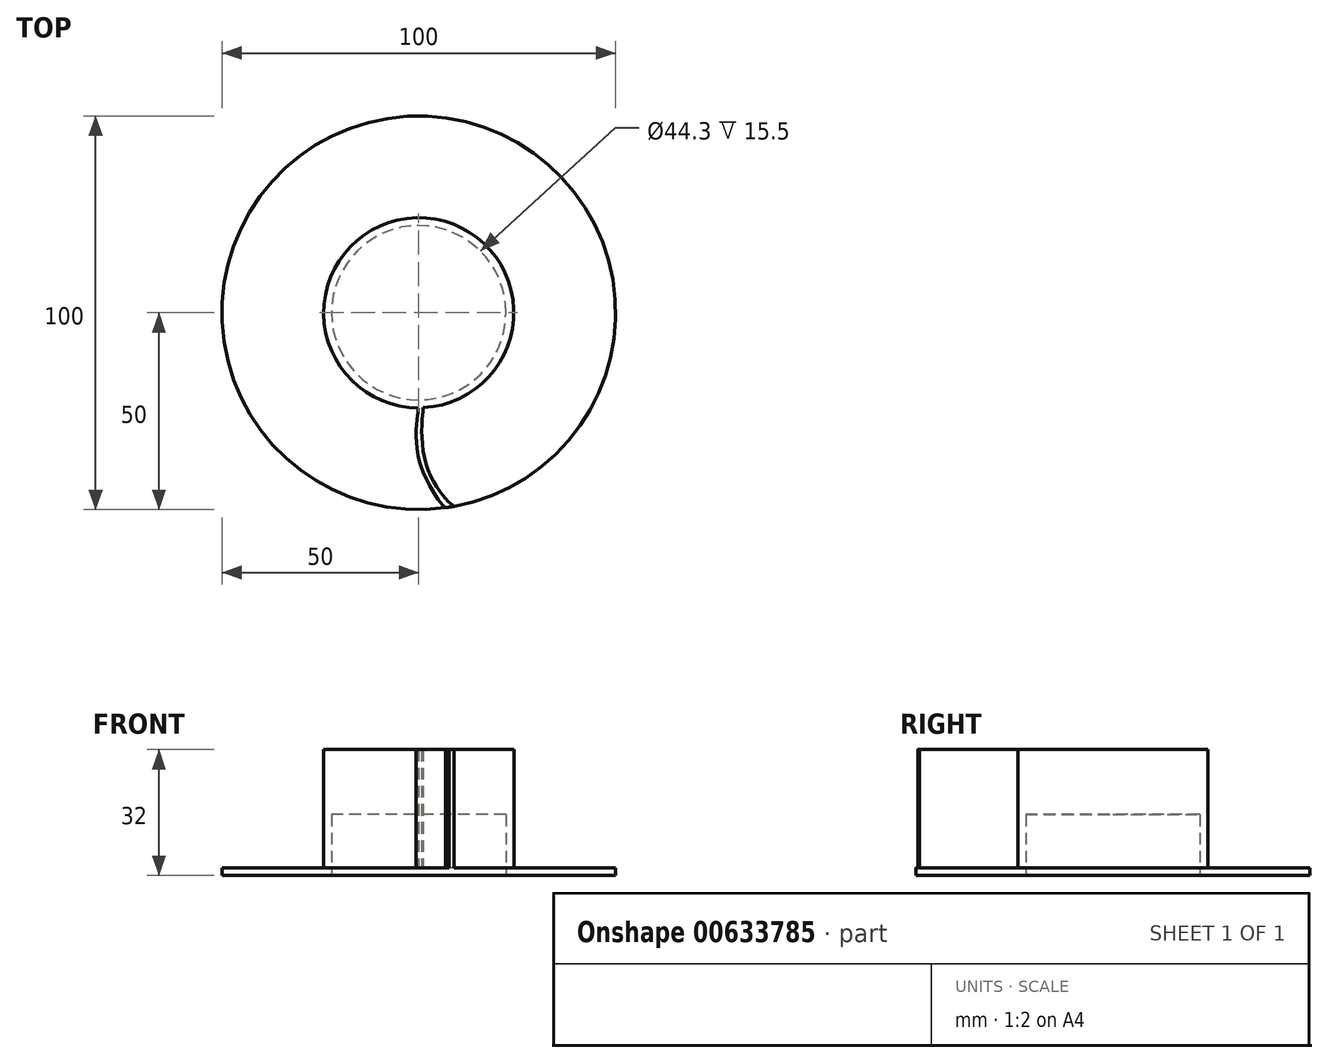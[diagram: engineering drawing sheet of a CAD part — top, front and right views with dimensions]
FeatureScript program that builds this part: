
annotation { "Feature Type Name" : "Feature", "Feature Type Description" : "" }
export const myFeature = defineFeature(function(context is Context, id is Id, definition is map)
    precondition{}
    {
        {
            var Q0;
            Q0=qCreatedBy(makeId("Top.planeOp"),FACE);
            var sketch = newSketch(context, id + "F0", { "sketchPlane" : qUnion([Q0])});
            skCircle(sketch, "E0", {"center": v(0, 0) * mm, "radius": 22.15 * mm});
            skCircle(sketch, "E1.0", {"center": v(0, 0) * mm, "radius": 24.15 * mm});
            skCircle(sketch, "E2", {"center": v(0, 0) * mm, "radius": 50 * mm});
            skSolve(sketch);
        }
        {
            var Q0;
            Q0=makeQuery(id+"F0.imprint","IMPRINT",FACE,{"disambiguationData":[TD([[makeQuery(id+"F0.imprint","IMPRINT",EDGE,{"derivedFrom":sQuery(id+"F0.wireOp",EDGE,"E0")}),-1.0]])]});
            var Q1;
            Q1=makeQuery(id+"F0.imprint","IMPRINT",FACE,{"disambiguationData":[TD([[makeQuery(id+"F0.imprint","IMPRINT",EDGE,{"derivedFrom":sQuery(id+"F0.wireOp",EDGE,"E0")}),1.0]])]});
            extrude(context, id + "F1", {"entities" : qUnion([Q0, Q1]), "depth" : 17 * mm, "offsetDistance" : 25 * mm});
        }
        {
            var Q0;
            Q0=makeQuery(id+"F0.imprint","IMPRINT",FACE,{"disambiguationData":[TD([[makeQuery(id+"F0.imprint","IMPRINT",EDGE,{"derivedFrom":sQuery(id+"F0.wireOp",EDGE,"E0")}),1.0]])]});
            extrude(context, id + "F2", {"entities" : qUnion([Q0]), "operationType" : NewBodyOperationType.REMOVE, "depth" : 15.5 * mm, "offsetDistance" : 25 * mm});
        }
        {
            var Q0;
            Q0=makeQuery(id+"F0.imprint","IMPRINT",FACE,{"disambiguationData":[TD([[makeQuery(id+"F0.imprint","IMPRINT",EDGE,{"derivedFrom":sQuery(id+"F0.wireOp",EDGE,"E1.0")}),-1.0]])]});
            extrude(context, id + "F3", {"entities" : qUnion([Q0]), "operationType" : NewBodyOperationType.ADD, "depth" : 2 * mm, "offsetDistance" : 25 * mm});
        }
        {
            var Q0;
            Q0=makeQuery(id+"F3.opExtrude","CAP_FACE",FACE,{"disambiguationData":[OSD([sQuery(id+"F0.wireOp",EDGE,"E1.0"),sQuery(id+"F0.wireOp",EDGE,"E2")])],"isStart":false});
            var sketch = newSketch(context, id + "F4", { "sketchPlane" : qUnion([Q0])});
            skFitSpline(sketch, "E3", {"points": [v(0, -24.15) * mm, v(-0.02, -24.17) * mm, v(0, -36.96) * mm, v(6.75, -49.54) * mm, v(6.98, -49.51) * mm, v(8.9, -49.2) * mm, v(8.36, -48.7) * mm, v(1.49, -37.1) * mm, v(1.14, -24.12) * mm, v(1.11, -24.08) * mm, v(0, -24.15) * mm]});
            skSolve(sketch);
        }
        {
            var Q0;
            {var subQ0=sQuery(id+"F4.wireOp",EDGE,"E3");var subQ1=makeQuery(id+"F3.opExtrude","CAP_EDGE",EDGE,{"disambiguationData":[OSD([sQuery(id+"F0.wireOp",EDGE,"E2")])],"isStart":false});var subQ2=makeQuery(id+"F4.imprint","INTERSECT",VERTEX,{"disambiguationData":[OD(0.0)],"derivedFrom":[subQ1,subQ0]});Q0=makeQuery(id+"F4.imprint","IMPRINT",FACE,{"disambiguationData":[TD([[makeQuery(id+"F4.imprint","IMPRINT",EDGE,{"disambiguationData":[TD([[subQ2,1.0]])],"derivedFrom":subQ0}),1.0]])]});}
            var Q1;
            Q1=makeQuery(id+"FbTs9hMTHk68URn_1.1.F4.imprint","IMPRINT",FACE,{"disambiguationData":[TD([[makeQuery(id+"FbTs9hMTHk68URn_1.1.F4.imprint","IMPRINT",EDGE,{"derivedFrom":sQuery(id+"FbTs9hMTHk68URn_1.1.F4.wireOp",EDGE,"E3")}),1.0]])]});
            var Q2;
            Q2=makeQuery(id+"FbTs9hMTHk68URn_1.2.F4.imprint","IMPRINT",FACE,{"disambiguationData":[TD([[makeQuery(id+"FbTs9hMTHk68URn_1.2.F4.imprint","IMPRINT",EDGE,{"derivedFrom":sQuery(id+"FbTs9hMTHk68URn_1.2.F4.wireOp",EDGE,"E3")}),1.0]])]});
            var Q3;
            Q3=makeQuery(id+"FbTs9hMTHk68URn_1.3.F4.imprint","IMPRINT",FACE,{"disambiguationData":[TD([[makeQuery(id+"FbTs9hMTHk68URn_1.3.F4.imprint","IMPRINT",EDGE,{"derivedFrom":sQuery(id+"FbTs9hMTHk68URn_1.3.F4.wireOp",EDGE,"E3")}),1.0]])]});
            var Q4;
            Q4=makeQuery(id+"FbTs9hMTHk68URn_1.4.F4.imprint","IMPRINT",FACE,{"disambiguationData":[TD([[makeQuery(id+"FbTs9hMTHk68URn_1.4.F4.imprint","IMPRINT",EDGE,{"derivedFrom":sQuery(id+"FbTs9hMTHk68URn_1.4.F4.wireOp",EDGE,"E3")}),1.0]])]});
            var Q5;
            Q5=makeQuery(id+"FbTs9hMTHk68URn_1.5.F4.imprint","IMPRINT",FACE,{"disambiguationData":[TD([[makeQuery(id+"FbTs9hMTHk68URn_1.5.F4.imprint","IMPRINT",EDGE,{"derivedFrom":sQuery(id+"FbTs9hMTHk68URn_1.5.F4.wireOp",EDGE,"E3")}),1.0]])]});
            var Q6;
            Q6=makeQuery(id+"FbTs9hMTHk68URn_1.6.F4.imprint","IMPRINT",FACE,{"disambiguationData":[TD([[makeQuery(id+"FbTs9hMTHk68URn_1.6.F4.imprint","IMPRINT",EDGE,{"derivedFrom":sQuery(id+"FbTs9hMTHk68URn_1.6.F4.wireOp",EDGE,"E3")}),1.0]])]});
            var Q7;
            Q7=makeQuery(id+"FbTs9hMTHk68URn_1.8.F4.imprint","IMPRINT",FACE,{"disambiguationData":[TD([[makeQuery(id+"FbTs9hMTHk68URn_1.8.F4.imprint","IMPRINT",EDGE,{"derivedFrom":sQuery(id+"FbTs9hMTHk68URn_1.8.F4.wireOp",EDGE,"E3")}),1.0]])]});
            var Q8;
            Q8=makeQuery(id+"FbTs9hMTHk68URn_1.9.F4.imprint","IMPRINT",FACE,{"disambiguationData":[TD([[makeQuery(id+"FbTs9hMTHk68URn_1.9.F4.imprint","IMPRINT",EDGE,{"derivedFrom":sQuery(id+"FbTs9hMTHk68URn_1.9.F4.wireOp",EDGE,"E3")}),1.0]])]});
            var Q9;
            Q9=makeQuery(id+"FbTs9hMTHk68URn_1.7.F4.imprint","IMPRINT",FACE,{"disambiguationData":[TD([[makeQuery(id+"FbTs9hMTHk68URn_1.7.F4.imprint","IMPRINT",EDGE,{"derivedFrom":sQuery(id+"FbTs9hMTHk68URn_1.7.F4.wireOp",EDGE,"E3")}),1.0]])]});
            var Q10;
            Q10=makeQuery(id+"FbTs9hMTHk68URn_1.10.F4.imprint","IMPRINT",FACE,{"disambiguationData":[TD([[makeQuery(id+"FbTs9hMTHk68URn_1.10.F4.imprint","IMPRINT",EDGE,{"derivedFrom":sQuery(id+"FbTs9hMTHk68URn_1.10.F4.wireOp",EDGE,"E3")}),1.0]])]});
            var Q11;
            Q11=makeQuery(id+"FbTs9hMTHk68URn_1.11.F4.imprint","IMPRINT",FACE,{"disambiguationData":[TD([[makeQuery(id+"FbTs9hMTHk68URn_1.11.F4.imprint","IMPRINT",EDGE,{"derivedFrom":sQuery(id+"FbTs9hMTHk68URn_1.11.F4.wireOp",EDGE,"E3")}),1.0]])]});
            var Q12;
            Q12=makeQuery(id+"FbTs9hMTHk68URn_1.12.F4.imprint","IMPRINT",FACE,{"disambiguationData":[TD([[makeQuery(id+"FbTs9hMTHk68URn_1.12.F4.imprint","IMPRINT",EDGE,{"derivedFrom":sQuery(id+"FbTs9hMTHk68URn_1.12.F4.wireOp",EDGE,"E3")}),1.0]])]});
            var Q13;
            Q13=makeQuery(id+"FbTs9hMTHk68URn_1.13.F4.imprint","IMPRINT",FACE,{"disambiguationData":[TD([[makeQuery(id+"FbTs9hMTHk68URn_1.13.F4.imprint","IMPRINT",EDGE,{"derivedFrom":sQuery(id+"FbTs9hMTHk68URn_1.13.F4.wireOp",EDGE,"E3")}),1.0]])]});
            var Q14;
            Q14=makeQuery(id+"FbTs9hMTHk68URn_1.14.F4.imprint","IMPRINT",FACE,{"disambiguationData":[TD([[makeQuery(id+"FbTs9hMTHk68URn_1.14.F4.imprint","IMPRINT",EDGE,{"derivedFrom":sQuery(id+"FbTs9hMTHk68URn_1.14.F4.wireOp",EDGE,"E3")}),1.0]])]});
            var Q15;
            Q15=makeQuery(id+"FbTs9hMTHk68URn_1.15.F4.imprint","IMPRINT",FACE,{"disambiguationData":[TD([[makeQuery(id+"FbTs9hMTHk68URn_1.15.F4.imprint","IMPRINT",EDGE,{"derivedFrom":sQuery(id+"FbTs9hMTHk68URn_1.15.F4.wireOp",EDGE,"E3")}),1.0]])]});
            var Q16;
            Q16=makeQuery(id+"FbTs9hMTHk68URn_1.16.F4.imprint","IMPRINT",FACE,{"disambiguationData":[TD([[makeQuery(id+"FbTs9hMTHk68URn_1.16.F4.imprint","IMPRINT",EDGE,{"derivedFrom":sQuery(id+"FbTs9hMTHk68URn_1.16.F4.wireOp",EDGE,"E3")}),1.0]])]});
            var Q17;
            Q17=makeQuery(id+"FbTs9hMTHk68URn_1.17.F4.imprint","IMPRINT",FACE,{"disambiguationData":[TD([[makeQuery(id+"FbTs9hMTHk68URn_1.17.F4.imprint","IMPRINT",EDGE,{"derivedFrom":sQuery(id+"FbTs9hMTHk68URn_1.17.F4.wireOp",EDGE,"E3")}),1.0]])]});
            var Q18;
            Q18=makeQuery(id+"FbTs9hMTHk68URn_1.18.F4.imprint","IMPRINT",FACE,{"disambiguationData":[TD([[makeQuery(id+"FbTs9hMTHk68URn_1.18.F4.imprint","IMPRINT",EDGE,{"derivedFrom":sQuery(id+"FbTs9hMTHk68URn_1.18.F4.wireOp",EDGE,"E3")}),1.0]])]});
            var Q19;
            Q19=makeQuery(id+"FbTs9hMTHk68URn_1.19.F4.imprint","IMPRINT",FACE,{"disambiguationData":[TD([[makeQuery(id+"FbTs9hMTHk68URn_1.19.F4.imprint","IMPRINT",EDGE,{"derivedFrom":sQuery(id+"FbTs9hMTHk68URn_1.19.F4.wireOp",EDGE,"E3")}),1.0]])]});
            var Q20;
            Q20=makeQuery(id+"FbTs9hMTHk68URn_1.20.F4.imprint","IMPRINT",FACE,{"disambiguationData":[TD([[makeQuery(id+"FbTs9hMTHk68URn_1.20.F4.imprint","IMPRINT",EDGE,{"derivedFrom":sQuery(id+"FbTs9hMTHk68URn_1.20.F4.wireOp",EDGE,"E3")}),1.0]])]});
            var Q21;
            Q21=makeQuery(id+"FbTs9hMTHk68URn_1.22.F4.imprint","IMPRINT",FACE,{"disambiguationData":[TD([[makeQuery(id+"FbTs9hMTHk68URn_1.22.F4.imprint","IMPRINT",EDGE,{"derivedFrom":sQuery(id+"FbTs9hMTHk68URn_1.22.F4.wireOp",EDGE,"E3")}),1.0]])]});
            var Q22;
            Q22=makeQuery(id+"FbTs9hMTHk68URn_1.23.F4.imprint","IMPRINT",FACE,{"disambiguationData":[TD([[makeQuery(id+"FbTs9hMTHk68URn_1.23.F4.imprint","IMPRINT",EDGE,{"derivedFrom":sQuery(id+"FbTs9hMTHk68URn_1.23.F4.wireOp",EDGE,"E3")}),1.0]])]});
            var Q23;
            Q23=makeQuery(id+"FbTs9hMTHk68URn_1.21.F4.imprint","IMPRINT",FACE,{"disambiguationData":[TD([[makeQuery(id+"FbTs9hMTHk68URn_1.21.F4.imprint","IMPRINT",EDGE,{"derivedFrom":sQuery(id+"FbTs9hMTHk68URn_1.21.F4.wireOp",EDGE,"E3")}),1.0]])]});
            extrude(context, id + "F5", {"entities" : qUnion([Q0, Q1, Q2, Q3, Q4, Q5, Q6, Q7, Q8, Q9, Q10, Q11, Q12, Q13, Q14, Q15, Q16, Q17, Q18, Q19, Q20, Q21, Q22, Q23]), "operationType" : NewBodyOperationType.ADD, "depth" : 30 * mm, "offsetDistance" : 25 * mm});
        }
        {
            var Q0;
            Q0=makeQuery(id+"F1.opExtrude","CAP_FACE",FACE,{"disambiguationData":[OSD([sQuery(id+"F0.wireOp",EDGE,"E1.0")])],"isStart":false});
            extrude(context, id + "F6", {"entities" : qUnion([Q0]), "operationType" : NewBodyOperationType.ADD, "depth" : 15 * mm, "offsetDistance" : 25 * mm});
        }
    });
